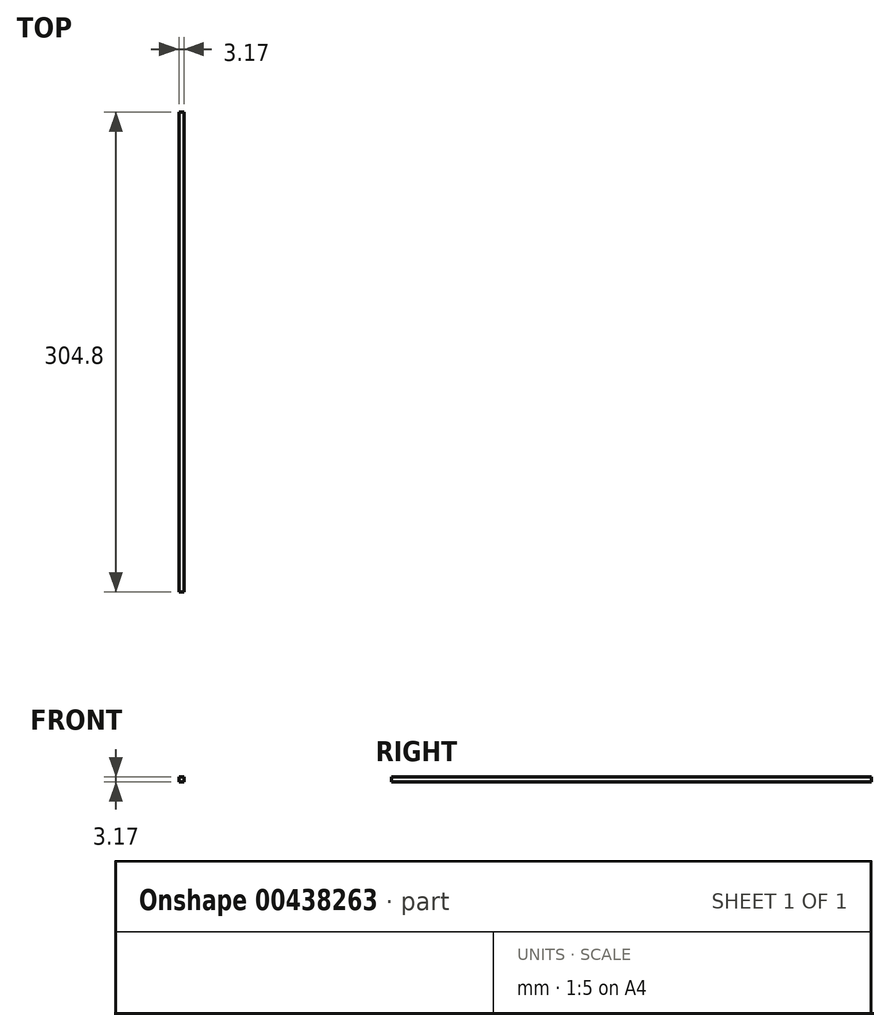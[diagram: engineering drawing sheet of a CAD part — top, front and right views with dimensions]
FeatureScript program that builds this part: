
annotation { "Feature Type Name" : "Feature", "Feature Type Description" : "" }
export const myFeature = defineFeature(function(context is Context, id is Id, definition is map)
    precondition{}
    {
        {
            var Q0;
            Q0=qCreatedBy(makeId("Right.planeOp"),FACE);
            var sketch = newSketch(context, id + "F0", { "sketchPlane" : qUnion([Q0])});
            skLineSegment(sketch, "E0.bottom", {"start": v(-170.47, 79.56) * mm, "end": v(134.33, 79.56) * mm});
            skLineSegment(sketch, "E0.top", {"start": v(-170.47, 76.39) * mm, "end": v(134.33, 76.39) * mm});
            skLineSegment(sketch, "E0.left", {"start": v(-170.47, 79.56) * mm, "end": v(-170.47, 76.39) * mm});
            skLineSegment(sketch, "E0.right", {"start": v(134.33, 79.56) * mm, "end": v(134.33, 76.39) * mm});
            skSolve(sketch);
        }
        {
            var Q0;
            Q0 = qSketchRegion(id + "F0", true);
            extrude(context, id + "F1", {"entities" : qUnion([Q0]), "depth" : 3.17 * mm});
        }
    });
